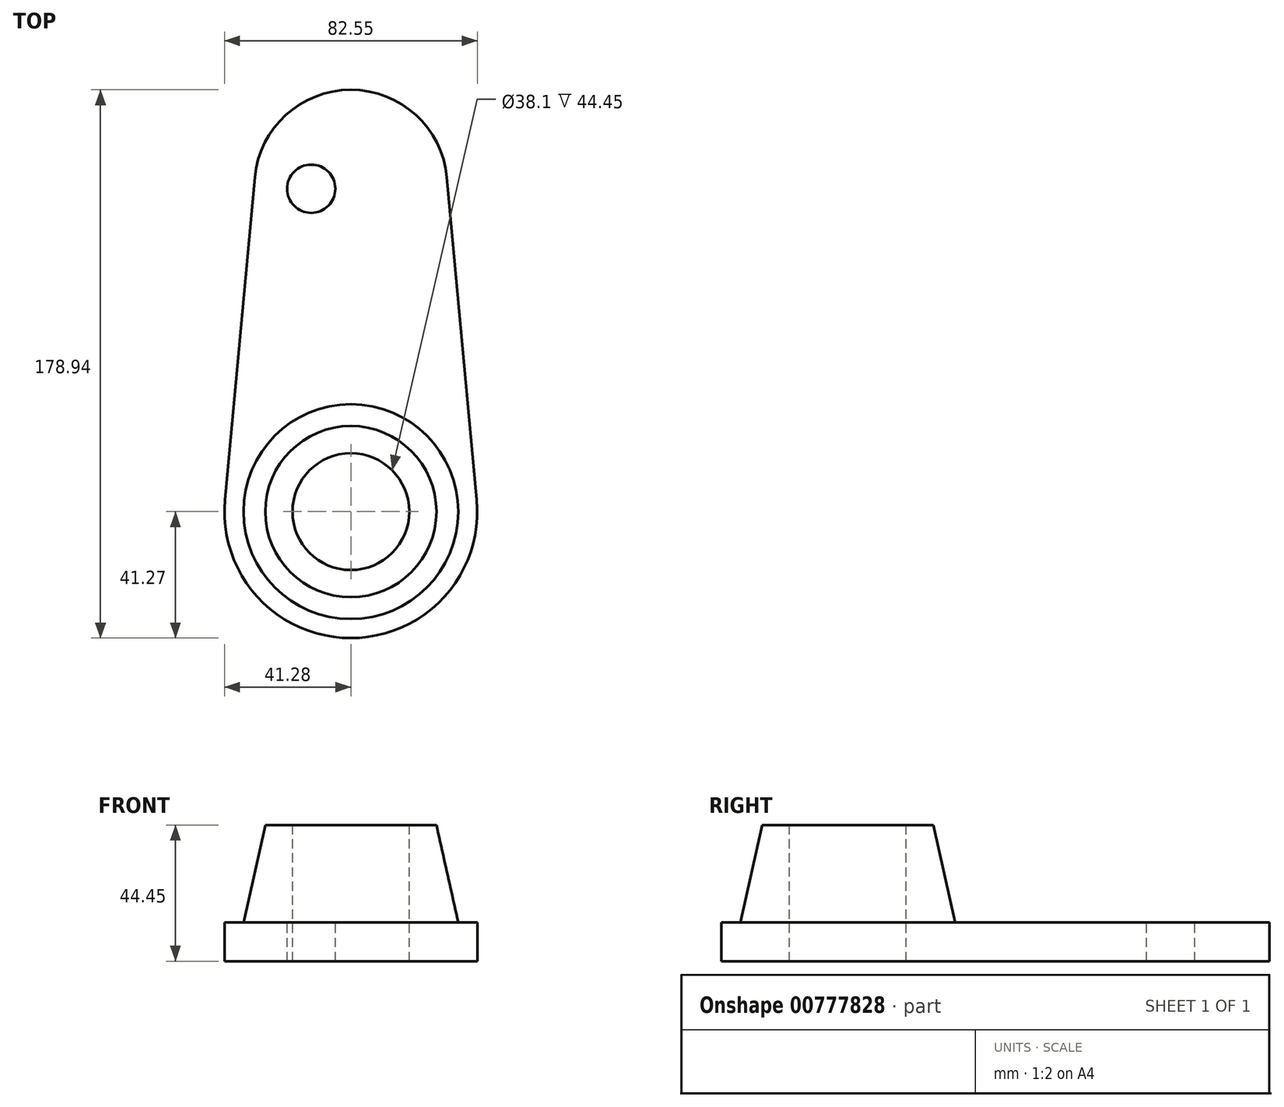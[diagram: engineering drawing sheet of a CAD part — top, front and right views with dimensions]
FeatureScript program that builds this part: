
annotation { "Feature Type Name" : "Feature", "Feature Type Description" : "" }
export const myFeature = defineFeature(function(context is Context, id is Id, definition is map)
    precondition{}
    {
        {
            var Q0;
            Q0=qCreatedBy(makeId("Top.planeOp"),FACE);
            var sketch = newSketch(context, id + "F0", { "sketchPlane" : qUnion([Q0])});
            skArc(sketch, "E0", {"start": v(-41.1, 3.8) * mm, "mid": v(0, -41.28) * mm, "end": v(41.1, 3.8) * mm});
            skLineSegment(sketch, "E1", {"start": v(0, 0) * mm, "end": v(0, 106.17) * mm, "construction": true});
            skArc(sketch, "E2", {"start": v(31.36, 109.07) * mm, "mid": v(0, 137.67) * mm, "end": v(-31.36, 109.07) * mm});
            skLineSegment(sketch, "E3", {"start": v(-31.36, 109.07) * mm, "end": v(-41.1, 3.8) * mm});
            skLineSegment(sketch, "E4", {"start": v(31.36, 109.07) * mm, "end": v(41.1, 3.8) * mm});
            skSolve(sketch);
        }
        {
            var Q0;
            Q0 = qSketchRegion(id + "F0", true);
            extrude(context, id + "F1", {"entities" : qUnion([Q0]), "depth" : 12.7 * mm, "offsetDistance" : 25.4 * mm});
        }
        {
            var Q0;
            Q0=qCreatedBy(makeId("Right.planeOp"),FACE);
            var sketch = newSketch(context, id + "F2", { "sketchPlane" : qUnion([Q0])});
            skLineSegment(sketch, "E5", {"start": v(-35.05, 12.7) * mm, "end": v(-27.94, 44.45) * mm});
            skLineSegment(sketch, "E6", {"start": v(-27.94, 44.45) * mm, "end": v(0, 44.45) * mm});
            skLineSegment(sketch, "E7", {"start": v(0, 44.45) * mm, "end": v(0, 12.7) * mm});
            skLineSegment(sketch, "E8", {"start": v(0, 12.7) * mm, "end": v(-35.05, 12.7) * mm});
            skSolve(sketch);
        }
        {
            var Q0;
            Q0 = qSketchRegion(id + "F2", true);
            var Q1;
            Q1=sQuery(id+"F2.wireOp",EDGE,"E7");
            revolve(context, id + "F3", {"operationType" : NewBodyOperationType.ADD, "surfaceOperationType" : NewSurfaceOperationType.NEW, "entities" : qUnion([Q0]), "axis" : qUnion([Q1]), "revolveType" : RevolveType.FULL});
        }
        {
            var Q0;
            Q0=makeQuery(id+"F3.opRevolve","SWEPT_FACE",FACE,{"disambiguationData":[OSD([sQuery(id+"F2.wireOp",EDGE,"E6")])]});
            var sketch = newSketch(context, id + "F4", { "sketchPlane" : qUnion([Q0])});
            skPoint(sketch, "E9", {"position": v(0, 0) * mm});
            skSolve(sketch);
        }
        {
            var Q0;
            Q0=sQuery(id+"F4.wireOp",VERTEX,"E9");
            var Q1;
            Q1=makeQuery(id+"F1.opExtrude","SWEPT_BODY",BODY,{"disambiguationData":[OSD([sQuery(id+"F0.wireOp",EDGE,"E0"),sQuery(id+"F0.wireOp",EDGE,"E2"),sQuery(id+"F0.wireOp",EDGE,"E3"),sQuery(id+"F0.wireOp",EDGE,"E4")])]});
            hole(context, id + "F5", {"style" : HoleStyle.SIMPLE, "endStyle" : HoleEndStyle.THROUGH, "holeDiameter" : 38.1 * mm, "majorDiameter" : 6.35 * mm, "isTappedThrough" : true, "tappedDepth" : 12.7 * mm, "tapClearance" : 3, "locations" : qUnion([Q0]), "scope" : qUnion([Q1])});
        }
        {
            var Q0;
            Q0=makeQuery(id+"F1.opExtrude","CAP_FACE",FACE,{"disambiguationData":[OSD([sQuery(id+"F0.wireOp",EDGE,"E0"),sQuery(id+"F0.wireOp",EDGE,"E2"),sQuery(id+"F0.wireOp",EDGE,"E3"),sQuery(id+"F0.wireOp",EDGE,"E4")])],"isStart":false});
            var sketch = newSketch(context, id + "F6", { "sketchPlane" : qUnion([Q0])});
            skPoint(sketch, "E10", {"position": v(-12.94, 105.38) * mm});
            skCircle(sketch, "E11", {"center": v(0, 0) * mm, "radius": 106.17 * mm, "construction": true});
            skLineSegment(sketch, "E12", {"start": v(0, 0) * mm, "end": v(-12.94, 105.38) * mm, "construction": true});
            skSolve(sketch);
        }
        {
            var Q0;
            Q0=sQuery(id+"F6.wireOp",VERTEX,"E10");
            var Q1;
            Q1=makeQuery(id+"F1.opExtrude","SWEPT_BODY",BODY,{"disambiguationData":[OSD([sQuery(id+"F0.wireOp",EDGE,"E0"),sQuery(id+"F0.wireOp",EDGE,"E2"),sQuery(id+"F0.wireOp",EDGE,"E3"),sQuery(id+"F0.wireOp",EDGE,"E4")])]});
            hole(context, id + "F7", {"style" : HoleStyle.SIMPLE, "endStyle" : HoleEndStyle.THROUGH, "holeDiameter" : 15.75 * mm, "majorDiameter" : 6.35 * mm, "isTappedThrough" : true, "tappedDepth" : 12.7 * mm, "tapClearance" : 3, "locations" : qUnion([Q0]), "scope" : qUnion([Q1])});
        }
    });
